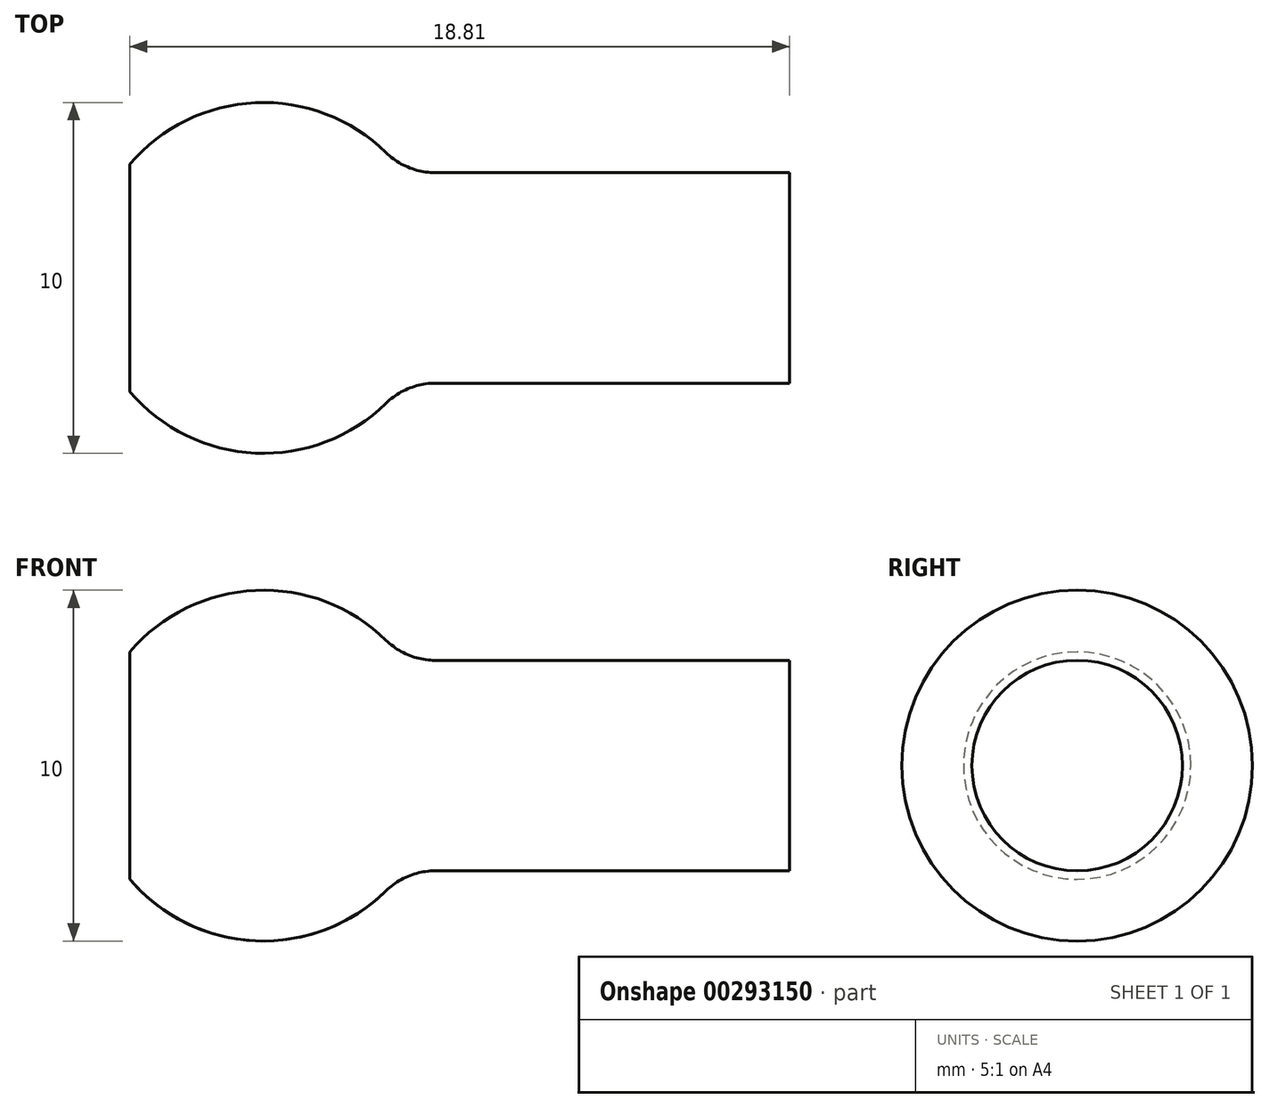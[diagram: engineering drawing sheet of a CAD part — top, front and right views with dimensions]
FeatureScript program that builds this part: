
annotation { "Feature Type Name" : "Feature", "Feature Type Description" : "" }
export const myFeature = defineFeature(function(context is Context, id is Id, definition is map)
    precondition{}
    {
        {
            var Q0;
            Q0=qCreatedBy(makeId("Front.planeOp"),FACE);
            var sketch = newSketch(context, id + "F0", { "sketchPlane" : qUnion([Q0])});
            skLineSegment(sketch, "E0", {"start": v(0, 0) * mm, "end": v(-18.8, 0) * mm});
            skLineSegment(sketch, "E1", {"start": v(0, 0) * mm, "end": v(0, -3) * mm});
            skLineSegment(sketch, "E2.0", {"start": v(0, -3) * mm, "end": v(-11, -3) * mm});
            skArc(sketch, "E3", {"start": v(-18.8, -3.24) * mm, "mid": v(-14.85, -5) * mm, "end": v(-11, -3) * mm});
            skLineSegment(sketch, "E4", {"start": v(-18.8, 0) * mm, "end": v(-18.8, -3.24) * mm});
            skSolve(sketch);
        }
        {
            var Q0;
            Q0=qSketchRegion(id+"F0",true);
            var Q1;
            Q1=sQuery(id+"F0.wireOp",EDGE,"E0");
            revolve(context, id + "F1", {"entities" : qUnion([Q0]), "axis" : qUnion([Q1]), "revolveType" : RevolveType.FULL});
        }
        {
            var Q0;
            Q0=makeQuery(id+"F1.opRevolve","SWEPT_EDGE",EDGE,{"disambiguationData":[OSD([sQuery(id+"F0.wireOp",EDGE,"E2.0"),sQuery(id+"F0.wireOp",EDGE,"E3")])]});
            fillet(context, id + "F2", {"entities" : qUnion([Q0]), "radius" : 2 * mm, "tangentPropagation" : true, "allowEdgeOverflow" : false});
        }
    });
